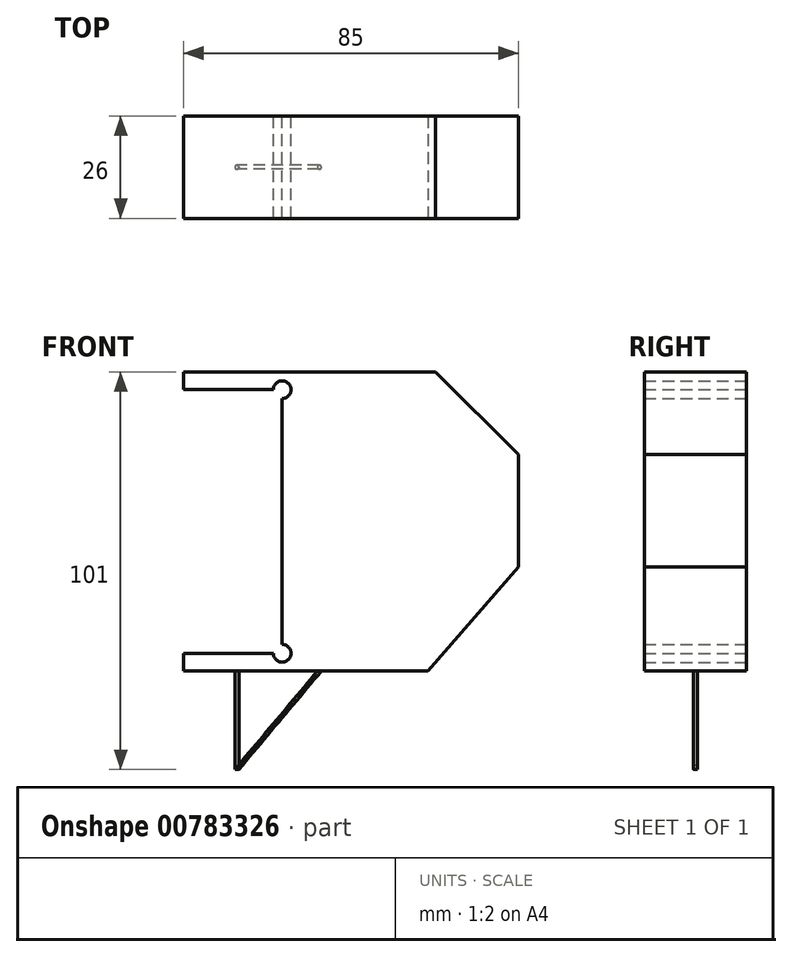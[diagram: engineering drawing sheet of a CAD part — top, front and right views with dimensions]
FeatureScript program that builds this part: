
annotation { "Feature Type Name" : "Feature", "Feature Type Description" : "" }
export const myFeature = defineFeature(function(context is Context, id is Id, definition is map)
    precondition{}
    {
        {
            var Q0;
            Q0=qCreatedBy(makeId("Front.planeOp"),FACE);
            var sketch = newSketch(context, id + "F0", { "sketchPlane" : qUnion([Q0])});
            skLineSegment(sketch, "E0.bottom", {"start": v(0, 0) * mm, "end": v(85, 0) * mm});
            skLineSegment(sketch, "E0.top", {"start": v(0, 76) * mm, "end": v(85, 76) * mm});
            skLineSegment(sketch, "E0.left", {"start": v(0, 0) * mm, "end": v(0, 76) * mm});
            skLineSegment(sketch, "E0.right", {"start": v(85, 0) * mm, "end": v(85, 76) * mm});
            skLineSegment(sketch, "E1", {"start": v(25, 76) * mm, "end": v(25, 0) * mm});
            skLineSegment(sketch, "E2.bottom", {"start": v(0, 71.5) * mm, "end": v(50, 71.5) * mm});
            skLineSegment(sketch, "E2.top", {"start": v(0, 4.5) * mm, "end": v(50, 4.5) * mm});
            skLineSegment(sketch, "E2.left", {"start": v(0, 71.5) * mm, "end": v(0, 4.5) * mm});
            skLineSegment(sketch, "E2.right", {"start": v(50, 71.5) * mm, "end": v(50, 4.5) * mm});
            skPoint(sketch, "E2.middle", {"position": v(25, 38) * mm});
            skCircle(sketch, "E3", {"center": v(25, 71.5) * mm, "radius": 2.25 * mm});
            skCircle(sketch, "E4", {"center": v(25, 4.5) * mm, "radius": 2.25 * mm});
            skSolve(sketch);
        }
        {
            var Q0;
            {var subQ0=sQuery(id+"F0.wireOp",EDGE,"E2.left");Q0=makeQuery(id+"F0.imprint","IMPRINT",FACE,{"disambiguationData":[TD([[makeQuery(id+"F0.imprint","IMPRINT",EDGE,{"derivedFrom":subQ0}),1.0]])]});}
            var Q1;
            {var subQ0=sQuery(id+"F0.wireOp",EDGE,"E2.right");Q1=makeQuery(id+"F0.imprint","IMPRINT",FACE,{"disambiguationData":[TD([[makeQuery(id+"F0.imprint","IMPRINT",EDGE,{"derivedFrom":subQ0}),-1.0]])]});}
            var Q2;
            {var subQ1=sQuery(id+"F0.wireOp",EDGE,"E0.left");var subQ7=sQuery(id+"F0.wireOp",EDGE,"E0.top");var subQ8=makeQuery(id+"F0.imprint","INTERSECT",VERTEX,{"derivedFrom":[subQ7,subQ1]});Q2=makeQuery(id+"F0.imprint","IMPRINT",FACE,{"disambiguationData":[TD([[makeQuery(id+"F0.imprint","IMPRINT",EDGE,{"disambiguationData":[TD([[subQ8,-1.0]])],"derivedFrom":subQ7}),-1.0]])]});}
            var Q3;
            {var subQ5=sQuery(id+"F0.wireOp",EDGE,"E0.right");Q3=makeQuery(id+"F0.imprint","IMPRINT",FACE,{"disambiguationData":[TD([[makeQuery(id+"F0.imprint","IMPRINT",EDGE,{"derivedFrom":subQ5}),1.0]])]});}
            var Q4;
            {var subQ1=sQuery(id+"F0.wireOp",EDGE,"E0.left");var subQ6=sQuery(id+"F0.wireOp",EDGE,"E0.bottom");var subQ9=makeQuery(id+"F0.imprint","INTERSECT",VERTEX,{"derivedFrom":[subQ6,subQ1]});Q4=makeQuery(id+"F0.imprint","IMPRINT",FACE,{"disambiguationData":[TD([[makeQuery(id+"F0.imprint","IMPRINT",EDGE,{"disambiguationData":[TD([[subQ9,-1.0]])],"derivedFrom":subQ6}),1.0]])]});}
            extrude(context, id + "F1", {"entities" : qUnion([Q0, Q1, Q2, Q3, Q4]), "depth" : 26 * mm, "offsetDistance" : 25 * mm});
        }
        {
            var Q0;
            Q0=makeQuery(id+"F1.opExtrude","SWEPT_FACE",FACE,{"disambiguationData":[OSD([sQuery(id+"F0.wireOp",EDGE,"E0.bottom")])]});
            var sketch = newSketch(context, id + "F2", { "sketchPlane" : qUnion([Q0])});
            skLineSegment(sketch, "E5", {"start": v(85, 13) * mm, "end": v(0, 13) * mm});
            skPoint(sketch, "E6", {"position": v(13.5, 13) * mm});
            skSolve(sketch);
        }
        {
            var Q0;
            Q0=makeQuery(id+"F1.opExtrude","SWEPT_EDGE",EDGE,{"disambiguationData":[OSD([sQuery(id+"F0.wireOp",EDGE,"E0.top"),sQuery(id+"F0.wireOp",EDGE,"E0.right")])]});
            cPoint(context, id + "F3", {"entities" : qUnion([Q0]), "parameter" : 0.5});
        }
        {
            var Q0;
            Q0=sQuery(id+"F2.wireOp",VERTEX,"E6");
            var Q1;
            Q1=sQuery(id+"F2.wireOp",VERTEX,"E5.end");
            var Q2;
            Q2 = qCreatedBy(id + "F3" ,VERTEX);
            cPlane(context, id + "F4", {"entities" : qUnion([Q0, Q1, Q2]), "cplaneType" : CPlaneType.THREE_POINT, "offset" : 25 * mm, "width" : 150 * mm, "height" : 150 * mm});
        }
        {
            var Q0;
            Q0=qCreatedBy(id+"F4.planeOp",FACE);
            var sketch = newSketch(context, id + "F5", { "sketchPlane" : qUnion([Q0])});
            skLineSegment(sketch, "E7", {"start": v(13.5, 0) * mm, "end": v(13.5, -25) * mm});
            skLineSegment(sketch, "E8", {"start": v(13.5, -25) * mm, "end": v(34.48, 0) * mm});
            skSolve(sketch);
        }
        {
            var Q0;
            Q0=sQuery(id+"F5.wireOp",VERTEX,"E7.end");
            var Q1;
            Q1=qCreatedBy(makeId("Top.planeOp"),FACE);
            cPlane(context, id + "F6", {"entities" : qUnion([Q0, Q1]), "cplaneType" : CPlaneType.PLANE_POINT, "offset" : 25 * mm, "width" : 150 * mm, "height" : 150 * mm});
        }
        {
            var Q0;
            Q0=qCreatedBy(id+"F6.planeOp",FACE);
            var sketch = newSketch(context, id + "F7", { "sketchPlane" : qUnion([Q0])});
            skCircle(sketch, "E9", {"center": v(13.5, -13) * mm, "radius": 0.5 * mm});
            skSolve(sketch);
        }
        {
            var Q0;
            Q0=makeQuery(id+"F7.imprint","IMPRINT",FACE,{"disambiguationData":[TD([[makeQuery(id+"F7.imprint","IMPRINT",EDGE,{"derivedFrom":sQuery(id+"F7.wireOp",EDGE,"E9")}),1.0]])]});
            var Q1;
            Q1=sQuery(id+"F5.wireOp",EDGE,"E7");
            sweep(context, id + "F8", {"operationType" : NewBodyOperationType.ADD, "profiles" : qUnion([Q0]), "path" : qUnion([Q1])});
        }
        {
            var Q0;
            Q0=makeQuery(id+"F1.opExtrude","CAP_FACE",FACE,{"disambiguationData":[OSD([sQuery(id+"F0.wireOp",EDGE,"E0.bottom"),sQuery(id+"F0.wireOp",EDGE,"E0.top"),sQuery(id+"F0.wireOp",EDGE,"E0.left"),sQuery(id+"F0.wireOp",EDGE,"E0.right"),sQuery(id+"F0.wireOp",EDGE,"E2.left"),sQuery(id+"F0.wireOp",EDGE,"E3"),sQuery(id+"F0.wireOp",EDGE,"E4")])],"isStart":false});
            var sketch = newSketch(context, id + "F9", { "sketchPlane" : qUnion([Q0])});
            skLineSegment(sketch, "E10", {"start": v(0, 76) * mm, "end": v(64, 76) * mm});
            skLineSegment(sketch, "E11", {"start": v(64, 76) * mm, "end": v(85, 55) * mm});
            skLineSegment(sketch, "E12", {"start": v(0, 0) * mm, "end": v(62, 0) * mm});
            skLineSegment(sketch, "E13", {"start": v(62, 0) * mm, "end": v(85, 26.38) * mm});
            skSolve(sketch);
        }
        {
            var Q0;
            Q0 = qSketchRegion(id + "F9", true);
            var Q1;
            {var subQ0=sQuery(id+"F9.wireOp",EDGE,"E11");Q1=makeQuery(id+"F9.imprint","IMPRINT",FACE,{"disambiguationData":[TD([[makeQuery(id+"F9.imprint","IMPRINT",EDGE,{"derivedFrom":subQ0}),1.0]])]});}
            var Q2;
            {var subQ0=sQuery(id+"F9.wireOp",EDGE,"E13");Q2=makeQuery(id+"F9.imprint","IMPRINT",FACE,{"disambiguationData":[TD([[makeQuery(id+"F9.imprint","IMPRINT",EDGE,{"derivedFrom":subQ0}),-1.0]])]});}
            var Q3;
            Q3=makeQuery(id+"F1.opExtrude","CAP_FACE",FACE,{"disambiguationData":[OSD([sQuery(id+"F0.wireOp",EDGE,"E0.bottom"),sQuery(id+"F0.wireOp",EDGE,"E0.top"),sQuery(id+"F0.wireOp",EDGE,"E0.left"),sQuery(id+"F0.wireOp",EDGE,"E0.right"),sQuery(id+"F0.wireOp",EDGE,"E2.left"),sQuery(id+"F0.wireOp",EDGE,"E3"),sQuery(id+"F0.wireOp",EDGE,"E4")])],"isStart":true});
            extrude(context, id + "F10", {"entities" : qUnion([Q0, Q1, Q2]), "operationType" : NewBodyOperationType.REMOVE, "endBound" : BoundingType.UP_TO_SURFACE, "oppositeDirection" : true, "depth" : 25 * mm, "endBoundEntityFace" : qUnion([Q3]), "offsetDistance" : 25 * mm});
        }
        {
            var Q0;
            Q0=makeQuery(id+"F8.opSweep","CAP_FACE",FACE,{"disambiguationData":[OSD([sQuery(id+"F5.wireOp",VERTEX,"E7.end"),sQuery(id+"F7.wireOp",EDGE,"E9")])],"isStart":true});
            var Q1;
            Q1=sQuery(id+"F5.wireOp",EDGE,"E8");
            sweep(context, id + "F11", {"operationType" : NewBodyOperationType.ADD, "profiles" : qUnion([Q0]), "path" : qUnion([Q1])});
        }
    });
